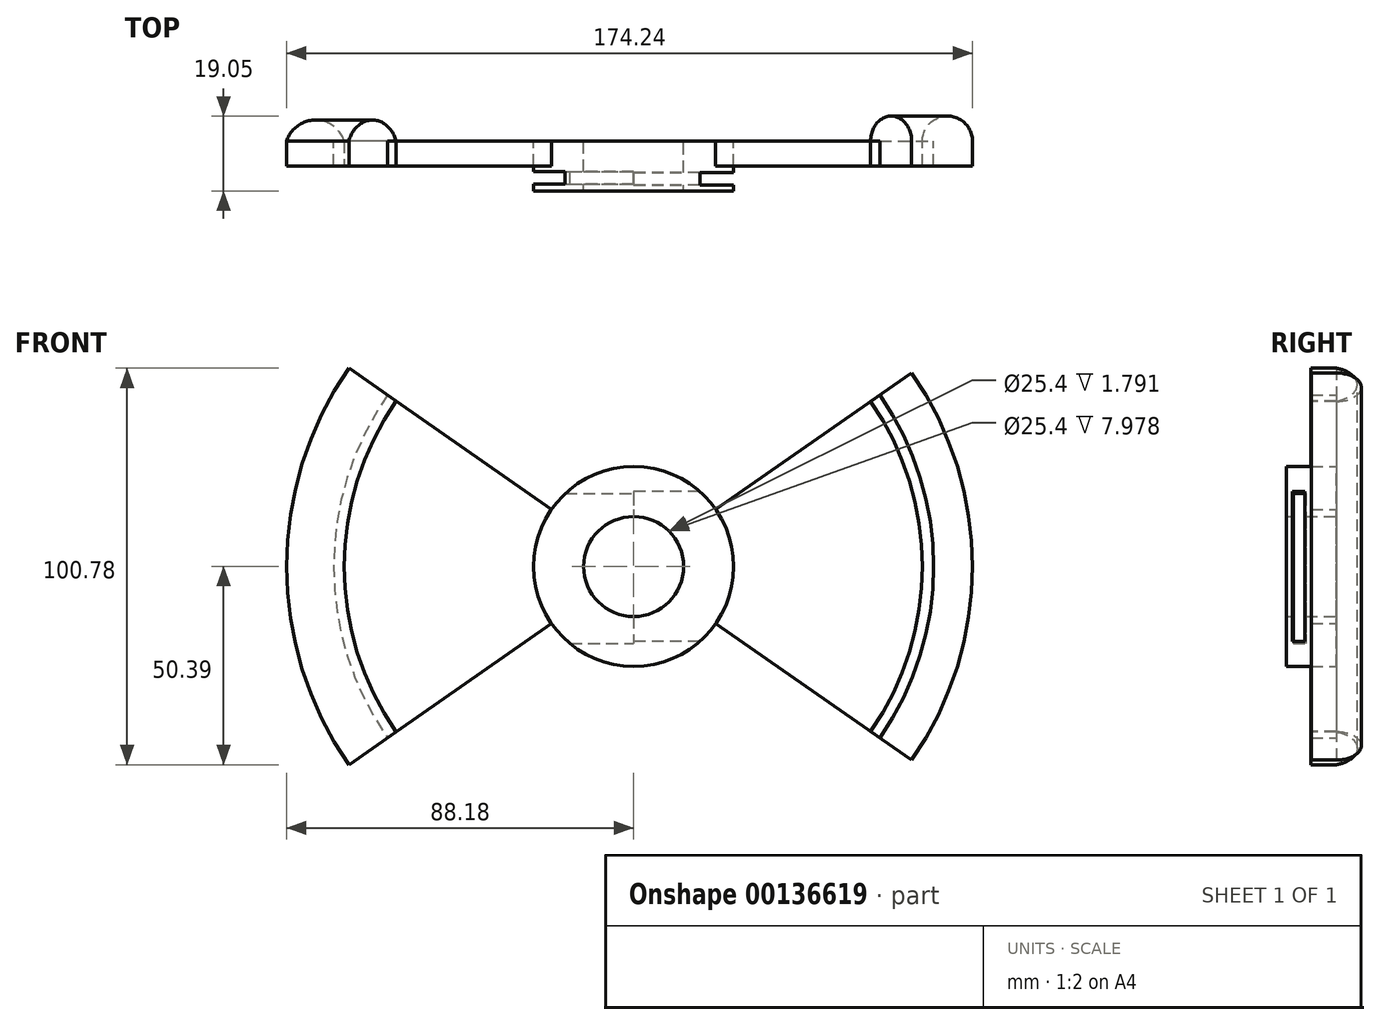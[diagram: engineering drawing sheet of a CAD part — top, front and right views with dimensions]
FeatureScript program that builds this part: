
annotation { "Feature Type Name" : "Feature", "Feature Type Description" : "" }
export const myFeature = defineFeature(function(context is Context, id is Id, definition is map)
    precondition{}
    {
        {
            var Q0;
            Q0=qCreatedBy(makeId("Front.planeOp"),FACE);
            var sketch = newSketch(context, id + "F0", { "sketchPlane" : qUnion([Q0])});
            skCircle(sketch, "E0", {"center": v(0, 0) * mm, "radius": 25.4 * mm});
            skLineSegment(sketch, "E1", {"start": v(-72.96, 50.8) * mm, "end": v(0, 0) * mm});
            skLineSegment(sketch, "E2", {"start": v(0, 0) * mm, "end": v(72.96, -50.8) * mm});
            skLineSegment(sketch, "E3", {"start": v(0, 0) * mm, "end": v(72.96, 50.8) * mm});
            skLineSegment(sketch, "E4", {"start": v(0, 0) * mm, "end": v(-72.96, -50.8) * mm});
            skCircle(sketch, "E5", {"center": v(0, 0) * mm, "radius": 12.7 * mm});
            skArc(sketch, "E6", {"start": v(-72.96, 50.8) * mm, "mid": v(-92.36, 0) * mm, "end": v(-72.96, -50.8) * mm});
            skArc(sketch, "E7", {"start": v(72.96, -50.8) * mm, "mid": v(92.36, 0) * mm, "end": v(72.96, 50.8) * mm});
            skLineSegment(sketch, "E8", {"start": v(-72.96, 50.8) * mm, "end": v(-62.53, 43.54) * mm});
            skLineSegment(sketch, "E9", {"start": v(72.96, 50.8) * mm, "end": v(62.53, 43.54) * mm});
            skArc(sketch, "E10", {"start": v(62.53, -43.54) * mm, "mid": v(76.2, 0) * mm, "end": v(62.53, 43.54) * mm});
            skArc(sketch, "E11", {"start": v(-62.53, 43.54) * mm, "mid": v(-76.2, 0) * mm, "end": v(-62.53, -43.54) * mm});
            skSolve(sketch);
        }
        {
            var Q0;
            {var subQ5=sQuery(id+"F0.wireOp",EDGE,"E11");Q0=makeQuery(id+"F0.imprint","IMPRINT",FACE,{"disambiguationData":[TD([[makeQuery(id+"F0.imprint","IMPRINT",EDGE,{"derivedFrom":subQ5}),1.0]])]});}
            var Q1;
            {var subQ5=sQuery(id+"F0.wireOp",EDGE,"E10");Q1=makeQuery(id+"F0.imprint","IMPRINT",FACE,{"disambiguationData":[TD([[makeQuery(id+"F0.imprint","IMPRINT",EDGE,{"derivedFrom":subQ5}),1.0]])]});}
            extrude(context, id + "F1", {"entities" : qUnion([Q0, Q1]), "depth" : 6.35 * mm});
        }
        {
            var Q0;
            {var subQ0=sQuery(id+"F0.wireOp",EDGE,"E1");var subQ1=sQuery(id+"F0.wireOp",EDGE,"E0");var subQ2=makeQuery(id+"F0.imprint","INTERSECT",VERTEX,{"derivedFrom":[subQ1,subQ0]});Q0=makeQuery(id+"F0.imprint","IMPRINT",FACE,{"disambiguationData":[TD([[makeQuery(id+"F0.imprint","IMPRINT",EDGE,{"disambiguationData":[TD([[subQ2,1.0]])],"derivedFrom":subQ1}),1.0]])]});}
            var Q1;
            {var subQ0=sQuery(id+"F0.wireOp",EDGE,"E1");var subQ1=sQuery(id+"F0.wireOp",EDGE,"E0");var subQ2=makeQuery(id+"F0.imprint","INTERSECT",VERTEX,{"derivedFrom":[subQ1,subQ0]});Q1=makeQuery(id+"F0.imprint","IMPRINT",FACE,{"disambiguationData":[TD([[makeQuery(id+"F0.imprint","IMPRINT",EDGE,{"disambiguationData":[TD([[subQ2,-1.0]])],"derivedFrom":subQ1}),1.0]])]});}
            var Q2;
            {var subQ0=sQuery(id+"F0.wireOp",EDGE,"E4");var subQ1=sQuery(id+"F0.wireOp",EDGE,"E0");var subQ2=makeQuery(id+"F0.imprint","INTERSECT",VERTEX,{"derivedFrom":[subQ1,subQ0]});Q2=makeQuery(id+"F0.imprint","IMPRINT",FACE,{"disambiguationData":[TD([[makeQuery(id+"F0.imprint","IMPRINT",EDGE,{"disambiguationData":[TD([[subQ2,-1.0]])],"derivedFrom":subQ1}),1.0]])]});}
            var Q3;
            {var subQ0=sQuery(id+"F0.wireOp",EDGE,"E3");var subQ1=sQuery(id+"F0.wireOp",EDGE,"E0");var subQ2=makeQuery(id+"F0.imprint","INTERSECT",VERTEX,{"derivedFrom":[subQ1,subQ0]});Q3=makeQuery(id+"F0.imprint","IMPRINT",FACE,{"disambiguationData":[TD([[makeQuery(id+"F0.imprint","IMPRINT",EDGE,{"disambiguationData":[TD([[subQ2,1.0]])],"derivedFrom":subQ1}),1.0]])]});}
            extrude(context, id + "F2", {"entities" : qUnion([Q0, Q1, Q2, Q3]), "depth" : 12.7 * mm});
        }
        {
            var Q0;
            Q0=sQuery(id+"F0.wireOp",VERTEX,"E8.start");
            var Q1;
            Q1=sQuery(id+"F0.wireOp",VERTEX,"E11.start");
            var Q2;
            Q2=makeQuery(id+"F1.opExtrude","CAP_VERTEX",VERTEX,{"disambiguationData":[OSD([sQuery(id+"F0.wireOp",EDGE,"E1"),sQuery(id+"F0.wireOp",EDGE,"E8"),sQuery(id+"F0.wireOp",EDGE,"E11")])],"isStart":false});
            cPlane(context, id + "F3", {"entities" : qUnion([Q0, Q1, Q2]), "cplaneType" : CPlaneType.THREE_POINT, "offset" : 25.4 * mm, "width" : 152.4 * mm, "height" : 152.4 * mm});
        }
        {
            var Q0;
            Q0=qCreatedBy(id+"F3.planeOp",FACE);
            var sketch = newSketch(context, id + "F4", { "sketchPlane" : qUnion([Q0])});
            skLineSegment(sketch, "E12", {"start": v(-73.53, -6.38) * mm, "end": v(-88.18, -6.38) * mm});
            skLineSegment(sketch, "E13", {"start": v(-88.18, 0) * mm, "end": v(-88.18, -6.38) * mm});
            skArc(sketch, "E14", {"start": v(-73.53, 0) * mm, "mid": v(-80.85, 5.35) * mm, "end": v(-88.18, 0) * mm});
            skLineSegment(sketch, "E15", {"start": v(-73.53, 0) * mm, "end": v(-73.53, -6.38) * mm});
            skSolve(sketch);
        }
        {
            var Q0;
            Q0 = qSketchRegion(id + "F4", true);
            var Q1;
            Q1=sQuery(id+"F0.wireOp",EDGE,"E11");
            sweep(context, id + "F5", {"profiles" : qUnion([Q0]), "path" : qUnion([Q1])});
        }
        {
            var Q0;
            Q0=sQuery(id+"F0.wireOp",VERTEX,"E7.end");
            var Q1;
            Q1=sQuery(id+"F0.wireOp",VERTEX,"E9.end");
            var Q2;
            Q2=makeQuery(id+"F1.opExtrude","CAP_VERTEX",VERTEX,{"disambiguationData":[OSD([sQuery(id+"F0.wireOp",EDGE,"E3"),sQuery(id+"F0.wireOp",EDGE,"E9"),sQuery(id+"F0.wireOp",EDGE,"E10")])],"isStart":false});
            cPlane(context, id + "F6", {"entities" : qUnion([Q0, Q1, Q2]), "cplaneType" : CPlaneType.THREE_POINT, "offset" : 25.4 * mm, "width" : 152.4 * mm, "height" : 152.4 * mm});
        }
        {
            var Q0;
            Q0=qCreatedBy(id+"F6.planeOp",FACE);
            var sketch = newSketch(context, id + "F7", { "sketchPlane" : qUnion([Q0])});
            skLineSegment(sketch, "E16", {"start": v(86.06, 0) * mm, "end": v(73.36, 0) * mm});
            skLineSegment(sketch, "E17", {"start": v(73.36, 0) * mm, "end": v(73.36, 6.35) * mm});
            skLineSegment(sketch, "E18", {"start": v(73.36, 6.35) * mm, "end": v(86.06, 6.35) * mm});
            skLineSegment(sketch, "E19", {"start": v(86.06, 6.35) * mm, "end": v(86.06, 0) * mm});
            skArc(sketch, "E20", {"start": v(73.36, 0) * mm, "mid": v(79.7, -6.35) * mm, "end": v(86.06, 0) * mm});
            skSolve(sketch);
        }
        {
            var Q0;
            Q0=makeQuery(id+"F7.imprint","IMPRINT",FACE,{"disambiguationData":[TD([[makeQuery(id+"F7.imprint","IMPRINT",EDGE,{"derivedFrom":sQuery(id+"F7.wireOp",EDGE,"E16")}),-1.0]])]});
            var Q1;
            Q1=makeQuery(id+"F7.imprint","IMPRINT",FACE,{"disambiguationData":[TD([[makeQuery(id+"F7.imprint","IMPRINT",EDGE,{"derivedFrom":sQuery(id+"F7.wireOp",EDGE,"E16")}),1.0]])]});
            var Q2;
            Q2=makeQuery(id+"F1.opExtrude","CAP_EDGE",EDGE,{"disambiguationData":[OSD([sQuery(id+"F0.wireOp",EDGE,"E10")])],"isStart":false});
            sweep(context, id + "F8", {"profiles" : qUnion([Q0, Q1]), "path" : qUnion([Q2])});
        }
        {
            var Q0;
            Q0=qCreatedBy(makeId("Right.planeOp"),FACE);
            var sketch = newSketch(context, id + "F9", { "sketchPlane" : qUnion([Q0])});
            skLineSegment(sketch, "E21.bottom", {"start": v(-11.17, 19.05) * mm, "end": v(-7.98, 19.05) * mm});
            skLineSegment(sketch, "E21.top", {"start": v(-11.17, -19.05) * mm, "end": v(-7.98, -19.05) * mm});
            skLineSegment(sketch, "E21.left", {"start": v(-11.17, 19.05) * mm, "end": v(-11.17, -19.05) * mm});
            skLineSegment(sketch, "E21.right", {"start": v(-7.98, 19.05) * mm, "end": v(-7.98, -19.05) * mm});
            skSolve(sketch);
        }
        {
            var Q0;
            Q0 = qSketchRegion(id + "F9", true);
            extrude(context, id + "F10", {"entities" : qUnion([Q0]), "operationType" : NewBodyOperationType.REMOVE, "depth" : 38.1 * mm});
        }
        {
            var Q0;
            Q0=qCreatedBy(makeId("Right.planeOp"),FACE);
            var sketch = newSketch(context, id + "F11", { "sketchPlane" : qUnion([Q0])});
            skLineSegment(sketch, "E22.bottom", {"start": v(-7.73, 18.5) * mm, "end": v(-10.9, 18.5) * mm});
            skLineSegment(sketch, "E22.top", {"start": v(-7.73, -19.6) * mm, "end": v(-10.9, -19.6) * mm});
            skLineSegment(sketch, "E22.left", {"start": v(-7.73, 18.5) * mm, "end": v(-7.73, -19.6) * mm});
            skLineSegment(sketch, "E22.right", {"start": v(-10.9, 18.5) * mm, "end": v(-10.9, -19.6) * mm});
            skSolve(sketch);
        }
        {
            var Q0;
            Q0 = qSketchRegion(id + "F11", true);
            extrude(context, id + "F12", {"entities" : qUnion([Q0]), "operationType" : NewBodyOperationType.REMOVE, "oppositeDirection" : true, "depth" : 38.1 * mm});
        }
    });
